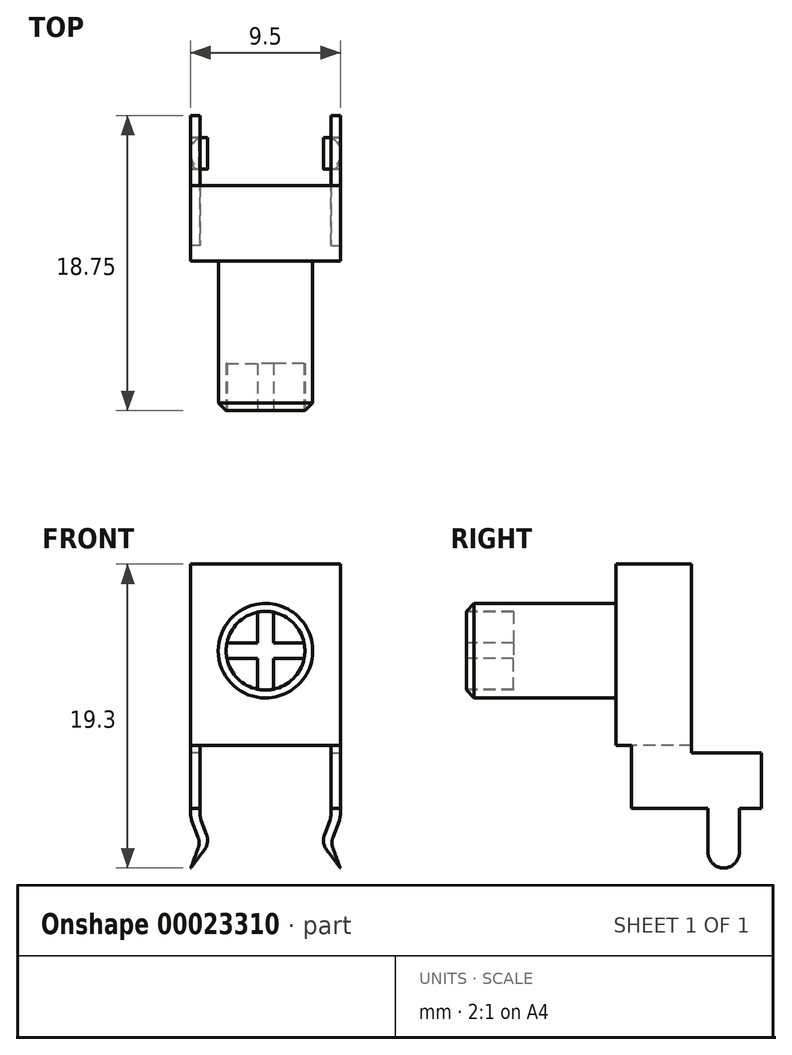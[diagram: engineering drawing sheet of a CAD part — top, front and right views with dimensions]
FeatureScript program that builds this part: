
annotation { "Feature Type Name" : "Feature", "Feature Type Description" : "" }
export const myFeature = defineFeature(function(context is Context, id is Id, definition is map)
    precondition{}
    {
        {
            var Q0;
            Q0=qCreatedBy(makeId("Front.planeOp"),FACE);
            var sketch = newSketch(context, id + "F0", { "sketchPlane" : qUnion([Q0])});
            skLineSegment(sketch, "E0", {"start": v(4.75, 0) * mm, "end": v(4.75, 5.5) * mm});
            skLineSegment(sketch, "E1", {"start": v(4.75, 5.5) * mm, "end": v(0, 5.5) * mm});
            skLineSegment(sketch, "E2", {"start": v(0, 5.5) * mm, "end": v(-4.75, 5.5) * mm});
            skLineSegment(sketch, "E3", {"start": v(-4.75, 5.5) * mm, "end": v(-4.75, -6) * mm});
            skLineSegment(sketch, "E4", {"start": v(-4.75, -6) * mm, "end": v(4.75, -6) * mm});
            skLineSegment(sketch, "E5", {"start": v(4.75, -6) * mm, "end": v(4.75, 0) * mm});
            skSolve(sketch);
        }
        {
            var Q0;
            Q0 = qSketchRegion(id + "F0", true);
            extrude(context, id + "F1", {"entities" : qUnion([Q0]), "oppositeDirection" : true, "depth" : 4.8 * mm});
        }
        {
            var Q0;
            Q0=makeQuery(id+"F1.opExtrude","SWEPT_FACE",FACE,{"disambiguationData":[OSD([sQuery(id+"F0.wireOp",EDGE,"E0"),sQuery(id+"F0.wireOp",EDGE,"E5")])]});
            var sketch = newSketch(context, id + "F2", { "sketchPlane" : qUnion([Q0])});
            skLineSegment(sketch, "E6", {"start": v(1, -10) * mm, "end": v(9.25, -10) * mm});
            skLineSegment(sketch, "E7", {"start": v(9.25, -10) * mm, "end": v(9.25, -6.5) * mm});
            skLineSegment(sketch, "E8", {"start": v(9.25, -6.5) * mm, "end": v(4.8, -6.5) * mm});
            skLineSegment(sketch, "E9", {"start": v(4.8, -6.5) * mm, "end": v(4.8, -6) * mm});
            skLineSegment(sketch, "E10", {"start": v(1, -10) * mm, "end": v(1, -6) * mm});
            skLineSegment(sketch, "E11", {"start": v(1, -6) * mm, "end": v(4.8, -6) * mm});
            skSolve(sketch);
        }
        {
            var Q0;
            Q0 = qSketchRegion(id + "F2", true);
            extrude(context, id + "F3", {"entities" : qUnion([Q0]), "oppositeDirection" : true, "depth" : 0.6 * mm});
        }
        {
            var Q0;
            Q0=qCreatedBy(makeId("Front.planeOp"),FACE);
            cPlane(context, id + "F4", {"entities" : qUnion([Q0]), "cplaneType" : CPlaneType.OFFSET, "offset" : 5.85 * mm, "oppositeDirection" : true, "width" : 150 * mm, "height" : 150 * mm});
        }
        {
            var Q0;
            Q0=qCreatedBy(id+"F4.planeOp",FACE);
            var sketch = newSketch(context, id + "F5", { "sketchPlane" : qUnion([Q0])});
            skLineSegment(sketch, "E12", {"start": v(4.15, -10) * mm, "end": v(4.15, -10.6) * mm});
            skLineSegment(sketch, "E13", {"start": v(4.15, -10.6) * mm, "end": v(3.55, -12.2) * mm});
            skLineSegment(sketch, "E14", {"start": v(3.55, -12.2) * mm, "end": v(4.75, -13.8) * mm});
            skLineSegment(sketch, "E15", {"start": v(4.75, -13.8) * mm, "end": v(4.15, -12.2) * mm});
            skLineSegment(sketch, "E16", {"start": v(4.15, -12.2) * mm, "end": v(4.75, -10.6) * mm});
            skLineSegment(sketch, "E17", {"start": v(4.75, -10.6) * mm, "end": v(4.75, -10) * mm});
            skLineSegment(sketch, "E18", {"start": v(4.75, -10) * mm, "end": v(4.15, -10) * mm});
            skSolve(sketch);
        }
        {
            var Q0;
            Q0 = qSketchRegion(id + "F5", true);
            extrude(context, id + "F6", {"entities" : qUnion([Q0]), "operationType" : NewBodyOperationType.ADD, "oppositeDirection" : true, "depth" : 2 * mm});
        }
        {
            var Q0;
            Q0=makeQuery(id+"F6.boolean.opBoolean","MERGE",FACE,{"derivedFrom":[makeQuery(id+"F3.opExtrude","CAP_FACE",FACE,{"disambiguationData":[OSD([sQuery(id+"F2.wireOp",EDGE,"E6"),sQuery(id+"F2.wireOp",EDGE,"E7"),sQuery(id+"F2.wireOp",EDGE,"E8"),sQuery(id+"F2.wireOp",EDGE,"E9"),sQuery(id+"F2.wireOp",EDGE,"E10"),sQuery(id+"F2.wireOp",EDGE,"E11")])],"isStart":true}),makeQuery(id+"F6.opExtrude","SWEPT_FACE",FACE,{"disambiguationData":[OSD([sQuery(id+"F5.wireOp",EDGE,"E17")])]})]});
            var sketch = newSketch(context, id + "F7", { "sketchPlane" : qUnion([Q0])});
            skLineSegment(sketch, "E19", {"start": v(5.85, -10.6) * mm, "end": v(5.85, -13.8) * mm, "construction": true});
            skLineSegment(sketch, "E20", {"start": v(7.85, -10.6) * mm, "end": v(7.85, -13.8) * mm, "construction": true});
            skLineSegment(sketch, "E21", {"start": v(5.85, -13.8) * mm, "end": v(7.85, -13.8) * mm});
            skArc(sketch, "E22", {"start": v(5.85, -12.8) * mm, "mid": v(6.85, -13.8) * mm, "end": v(7.85, -12.8) * mm});
            skLineSegment(sketch, "E23", {"start": v(5.85, -13.8) * mm, "end": v(5.85, -12.8) * mm});
            skLineSegment(sketch, "E24", {"start": v(7.85, -12.8) * mm, "end": v(7.85, -13.8) * mm});
            skSolve(sketch);
        }
        {
            var Q0;
            Q0 = qSketchRegion(id + "F7", true);
            extrude(context, id + "F8", {"entities" : qUnion([Q0]), "operationType" : NewBodyOperationType.REMOVE, "oppositeDirection" : true, "depth" : 25 * mm});
        }
        {
            var Q0;
            Q0=makeQuery(id+"F6.opExtrude","SWEPT_EDGE",EDGE,{"disambiguationData":[OSD([sQuery(id+"F5.wireOp",EDGE,"E15"),sQuery(id+"F5.wireOp",EDGE,"E16")])]});
            var Q1;
            Q1=makeQuery(id+"F6.opExtrude","SWEPT_EDGE",EDGE,{"disambiguationData":[OSD([sQuery(id+"F5.wireOp",EDGE,"E13"),sQuery(id+"F5.wireOp",EDGE,"E14")])]});
            var Q2;
            Q2=makeQuery(id+"F6.opExtrude","SWEPT_EDGE",EDGE,{"disambiguationData":[OSD([sQuery(id+"F5.wireOp",EDGE,"E12"),sQuery(id+"F5.wireOp",EDGE,"E13")])]});
            var Q3;
            Q3=makeQuery(id+"F6.opExtrude","SWEPT_EDGE",EDGE,{"disambiguationData":[OSD([sQuery(id+"F5.wireOp",EDGE,"E16"),sQuery(id+"F5.wireOp",EDGE,"E17")])]});
            fillet(context, id + "F9", {"entities" : qUnion([Q0, Q1, Q2, Q3]), "radius" : 1 * mm, "tangentPropagation" : true, "allowEdgeOverflow" : false});
        }
        {
            var Q0;
            Q0=makeQuery(id+"F3.opExtrude","SWEPT_BODY",BODY,{"disambiguationData":[OSD([sQuery(id+"F2.wireOp",EDGE,"E6"),sQuery(id+"F2.wireOp",EDGE,"E7"),sQuery(id+"F2.wireOp",EDGE,"E8"),sQuery(id+"F2.wireOp",EDGE,"E9"),sQuery(id+"F2.wireOp",EDGE,"E10"),sQuery(id+"F2.wireOp",EDGE,"E11")])]});
            var Q1;
            Q1=qCreatedBy(makeId("Right.planeOp"),FACE);
            mirror(context, id + "F10", {"operationType" : NewBodyOperationType.ADD, "entities" : qUnion([Q0]), "mirrorPlane" : qUnion([Q1])});
        }
        {
            var Q0;
            Q0=makeQuery(id+"F1.opExtrude","CAP_FACE",FACE,{"disambiguationData":[OSD([sQuery(id+"F0.wireOp",EDGE,"E0"),sQuery(id+"F0.wireOp",EDGE,"E1"),sQuery(id+"F0.wireOp",EDGE,"E2"),sQuery(id+"F0.wireOp",EDGE,"E3"),sQuery(id+"F0.wireOp",EDGE,"E4"),sQuery(id+"F0.wireOp",EDGE,"E5")])],"isStart":true});
            var sketch = newSketch(context, id + "F11", { "sketchPlane" : qUnion([Q0])});
            skCircle(sketch, "E25", {"center": v(0, 0) * mm, "radius": 3 * mm});
            skSolve(sketch);
        }
        {
            var Q0;
            Q0 = qSketchRegion(id + "F11", true);
            extrude(context, id + "F12", {"entities" : qUnion([Q0]), "operationType" : NewBodyOperationType.ADD, "depth" : 9.5 * mm});
        }
        {
            var Q0;
            Q0=makeQuery(id+"F12.opExtrude","CAP_EDGE",EDGE,{"disambiguationData":[OSD([sQuery(id+"F11.wireOp",EDGE,"E25")])],"isStart":false});
            chamfer(context, id + "F13", {"entities" : qUnion([Q0]), "width" : 0.5 * mm, "tangentPropagation" : true});
        }
        {
            var Q0;
            Q0=makeQuery(id+"F12.opExtrude","CAP_FACE",FACE,{"disambiguationData":[OSD([sQuery(id+"F11.wireOp",EDGE,"E25")])],"isStart":false});
            var sketch = newSketch(context, id + "F14", { "sketchPlane" : qUnion([Q0])});
            skLineSegment(sketch, "E26", {"start": v(0.5, 2.45) * mm, "end": v(0.5, 0.5) * mm});
            skLineSegment(sketch, "E27", {"start": v(0.5, 0.5) * mm, "end": v(2.45, 0.5) * mm});
            skLineSegment(sketch, "E28", {"start": v(2.45, -0.5) * mm, "end": v(0.5, -0.5) * mm});
            skLineSegment(sketch, "E29", {"start": v(0.5, -0.5) * mm, "end": v(0.5, -2.45) * mm});
            skLineSegment(sketch, "E30", {"start": v(-0.5, -2.45) * mm, "end": v(-0.5, -0.5) * mm});
            skLineSegment(sketch, "E31", {"start": v(-0.5, -0.5) * mm, "end": v(-2.45, -0.5) * mm});
            skLineSegment(sketch, "E32", {"start": v(-2.45, 0.5) * mm, "end": v(-0.5, 0.5) * mm});
            skLineSegment(sketch, "E33", {"start": v(-0.5, 0.5) * mm, "end": v(-0.5, 2.45) * mm});
            skArc(sketch, "E34", {"start": v(-0.5, -2.45) * mm, "mid": v(0, -2.5) * mm, "end": v(0.5, -2.45) * mm});
            skArc(sketch, "E35", {"start": v(2.45, -0.5) * mm, "mid": v(2.5, 0) * mm, "end": v(2.45, 0.5) * mm});
            skArc(sketch, "E36", {"start": v(0.5, 2.45) * mm, "mid": v(0, 2.5) * mm, "end": v(-0.5, 2.45) * mm});
            skArc(sketch, "E37", {"start": v(-2.45, 0.5) * mm, "mid": v(-2.5, 0) * mm, "end": v(-2.45, -0.5) * mm});
            skSolve(sketch);
        }
        {
            var Q0;
            Q0 = qSketchRegion(id + "F14", true);
            extrude(context, id + "F15", {"entities" : qUnion([Q0]), "operationType" : NewBodyOperationType.REMOVE, "oppositeDirection" : true, "depth" : 3 * mm});
        }
    });
